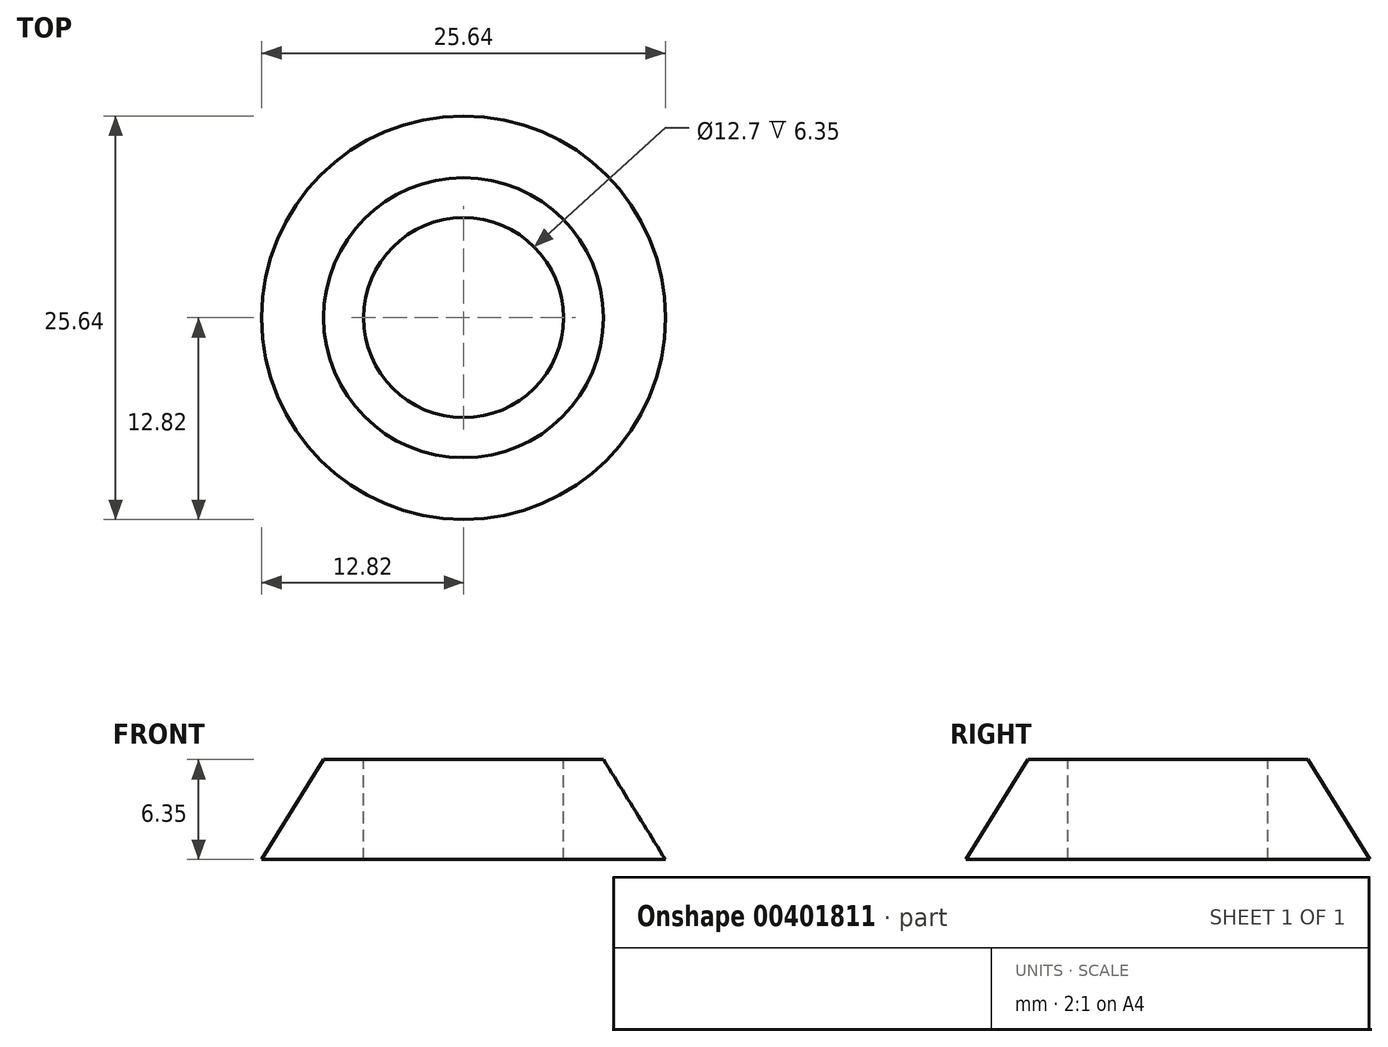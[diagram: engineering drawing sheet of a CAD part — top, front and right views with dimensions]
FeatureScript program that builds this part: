
annotation { "Feature Type Name" : "Feature", "Feature Type Description" : "" }
export const myFeature = defineFeature(function(context is Context, id is Id, definition is map)
    precondition{}
    {
        {
            var Q0;
            Q0=qCreatedBy(makeId("Top.planeOp"),FACE);
            var sketch = newSketch(context, id + "F0", { "sketchPlane" : qUnion([Q0])});
            skCircle(sketch, "E0", {"center": v(0, 0) * mm, "radius": 12.82 * mm});
            skSolve(sketch);
        }
        {
            var Q0;
            Q0=qCreatedBy(makeId("Top.planeOp"),FACE);
            cPlane(context, id + "F1", {"entities" : qUnion([Q0]), "cplaneType" : CPlaneType.OFFSET, "offset" : 6.35 * mm, "width" : 152.4 * mm, "height" : 152.4 * mm});
        }
        {
            var Q0;
            Q0=qCreatedBy(id+"F1.planeOp",FACE);
            var sketch = newSketch(context, id + "F2", { "sketchPlane" : qUnion([Q0])});
            skCircle(sketch, "E1", {"center": v(0, 0) * mm, "radius": 8.9 * mm});
            skSolve(sketch);
        }
        {
            var Q0;
            Q0=makeQuery(id+"F0.imprint","IMPRINT",FACE,{"disambiguationData":[TD([[makeQuery(id+"F0.imprint","IMPRINT",EDGE,{"derivedFrom":sQuery(id+"F0.wireOp",EDGE,"E0")}),1.0]])]});
            var Q1;
            Q1=makeQuery(id+"F2.imprint","IMPRINT",FACE,{"disambiguationData":[TD([[makeQuery(id+"F2.imprint","IMPRINT",EDGE,{"derivedFrom":sQuery(id+"F2.wireOp",EDGE,"E1")}),1.0]])]});
            loft(context, id + "F3", {"sheetProfilesArray" : [{ "sheetProfileEntities" : qUnion([Q0]) }, { "sheetProfileEntities" : qUnion([Q1]) }]});
        }
        {
            var Q0;
            Q0=qCreatedBy(id+"F1.planeOp",FACE);
            var sketch = newSketch(context, id + "F4", { "sketchPlane" : qUnion([Q0])});
            skCircle(sketch, "E2", {"center": v(0, 0) * mm, "radius": 6.35 * mm});
            skSolve(sketch);
        }
        {
            var Q0;
            Q0=makeQuery(id+"F4.imprint","IMPRINT",FACE,{"disambiguationData":[TD([[makeQuery(id+"F4.imprint","IMPRINT",EDGE,{"derivedFrom":sQuery(id+"F4.wireOp",EDGE,"E2")}),1.0]])]});
            extrude(context, id + "F5", {"entities" : qUnion([Q0]), "operationType" : NewBodyOperationType.REMOVE, "oppositeDirection" : true, "depth" : 25.4 * mm});
        }
    });
